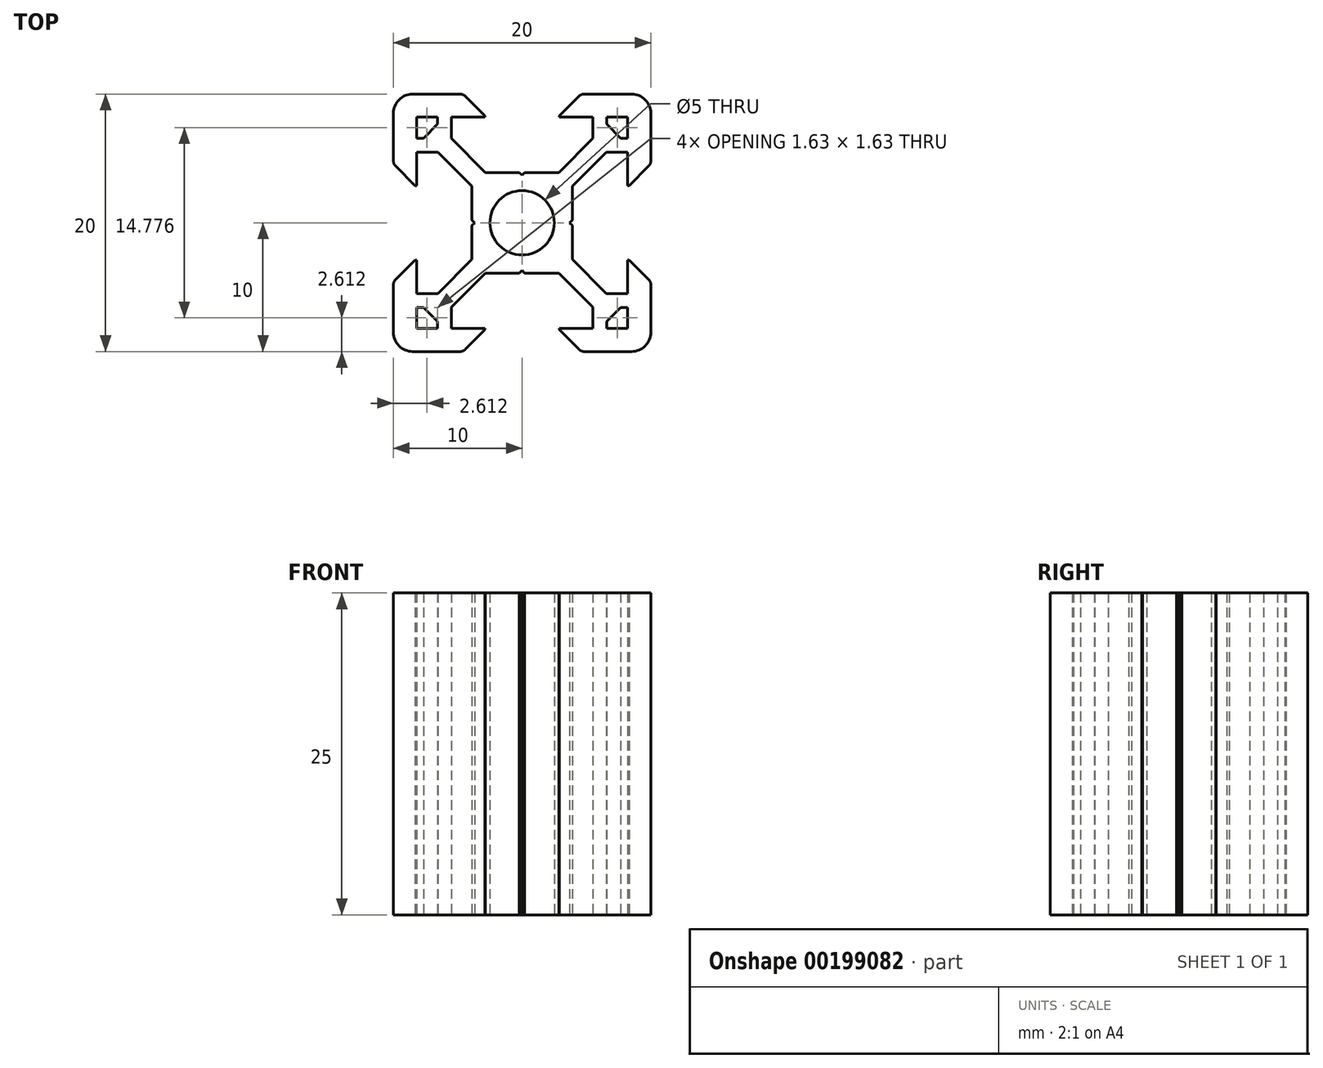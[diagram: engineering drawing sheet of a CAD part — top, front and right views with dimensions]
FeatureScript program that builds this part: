
annotation { "Feature Type Name" : "Feature", "Feature Type Description" : "" }
export const myFeature = defineFeature(function(context is Context, id is Id, definition is map)
    precondition{}
    {
        {
            var Q0;
            Q0=qCreatedBy(makeId("Top.planeOp"),FACE);
            var sketch = newSketch(context, id + "F0", { "sketchPlane" : qUnion([Q0])});
            skLineSegment(sketch, "E0.4", {"start": v(-2.85, 3.9) * mm, "end": v(-0.2, 3.9) * mm});
            skArc(sketch, "E0.48", {"start": v(-4.4, 9.82) * mm, "mid": v(-4.6, 9.95) * mm, "end": v(-4.82, 10) * mm});
            skLineSegment(sketch, "E0.49", {"start": v(-5.5, 6.55) * mm, "end": v(-2.85, 3.9) * mm});
            skLineSegment(sketch, "E0.72", {"start": v(-6.57, 7.66) * mm, "end": v(-6.57, 8.2) * mm});
            skLineSegment(sketch, "E0.103", {"start": v(-2.89, 8.2) * mm, "end": v(-5.5, 8.2) * mm});
            skArc(sketch, "E0.110", {"start": v(-8.5, 10) * mm, "mid": v(-9.07, 9.89) * mm, "end": v(-9.56, 9.56) * mm});
            skLineSegment(sketch, "E0.124", {"start": v(-5.5, 8.2) * mm, "end": v(-5.5, 6.55) * mm});
            skLineSegment(sketch, "E0.201", {"start": v(-4.4, 9.82) * mm, "end": v(-2.89, 8.3) * mm});
            skCircle(sketch, "E0.222", {"center": v(0, 0) * mm, "radius": 2.5 * mm});
            skLineSegment(sketch, "E0.289", {"start": v(-8.5, 10) * mm, "end": v(-4.82, 10) * mm});
            skLineSegment(sketch, "E0.340", {"start": v(-2.89, 8.3) * mm, "end": v(-2.89, 8.2) * mm});
            skLineSegment(sketch, "E0.361", {"start": v(-6.57, 8.2) * mm, "end": v(-8.2, 8.2) * mm});
            skLineSegment(sketch, "E0.440", {"start": v(-0.2, 3.9) * mm, "end": v(0, 3.7) * mm});
            skLineSegment(sketch, "E1", {"start": v(0, 0) * mm, "end": v(-19.3, 19.3) * mm, "construction": true});
            skLineSegment(sketch, "E2", {"start": v(-6.57, 7.66) * mm, "end": v(-7.12, 7.12) * mm});
            skLineSegment(sketch, "E3.MirrorCS", {"start": v(-8.3, 2.89) * mm, "end": v(-8.2, 2.89) * mm});
            skLineSegment(sketch, "E4.MirrorCS", {"start": v(-3.9, 0.2) * mm, "end": v(-3.7, 0) * mm});
            skLineSegment(sketch, "E5.MirrorCS", {"start": v(-10, 8.5) * mm, "end": v(-10, 4.82) * mm});
            skLineSegment(sketch, "E6.MirrorCS", {"start": v(-9.82, 4.4) * mm, "end": v(-8.3, 2.89) * mm});
            skLineSegment(sketch, "E7.MirrorCS", {"start": v(-3.9, 2.85) * mm, "end": v(-3.9, 0.2) * mm});
            skLineSegment(sketch, "E8.MirrorCS", {"start": v(-8.2, 5.5) * mm, "end": v(-6.55, 5.5) * mm});
            skLineSegment(sketch, "E9.MirrorCS", {"start": v(-8.2, 6.57) * mm, "end": v(-8.2, 8.2) * mm});
            skLineSegment(sketch, "E10.MirrorCS", {"start": v(-7.66, 6.57) * mm, "end": v(-8.2, 6.57) * mm});
            skArc(sketch, "E11.MirrorCS", {"start": v(-9.82, 4.4) * mm, "mid": v(-9.95, 4.6) * mm, "end": v(-10, 4.82) * mm});
            skArc(sketch, "E12.MirrorCS", {"start": v(-10, 8.5) * mm, "mid": v(-9.89, 9.07) * mm, "end": v(-9.56, 9.56) * mm});
            skLineSegment(sketch, "E13.MirrorCS", {"start": v(-7.66, 6.57) * mm, "end": v(-7.12, 7.12) * mm});
            skLineSegment(sketch, "E14.MirrorCS", {"start": v(-8.2, 2.89) * mm, "end": v(-8.2, 5.5) * mm});
            skLineSegment(sketch, "E15.MirrorCS", {"start": v(-6.55, 5.5) * mm, "end": v(-3.9, 2.85) * mm});
            skLineSegment(sketch, "E16", {"start": v(0, 0) * mm, "end": v(0, 23.95) * mm, "construction": true});
            skLineSegment(sketch, "E17.MirrorCS", {"start": v(6.57, 7.66) * mm, "end": v(6.57, 8.2) * mm});
            skLineSegment(sketch, "E18.MirrorCS", {"start": v(2.89, 8.3) * mm, "end": v(2.89, 8.2) * mm});
            skLineSegment(sketch, "E19.MirrorCS", {"start": v(7.66, 6.57) * mm, "end": v(7.12, 7.12) * mm});
            skArc(sketch, "E20.MirrorCS", {"start": v(9.82, 4.4) * mm, "mid": v(9.95, 4.6) * mm, "end": v(10, 4.82) * mm});
            skLineSegment(sketch, "E21.MirrorCS", {"start": v(0.2, 3.9) * mm, "end": v(0, 3.7) * mm});
            skLineSegment(sketch, "E22.MirrorCS", {"start": v(7.66, 6.57) * mm, "end": v(8.2, 6.57) * mm});
            skLineSegment(sketch, "E23.MirrorCS", {"start": v(6.57, 7.66) * mm, "end": v(7.12, 7.12) * mm});
            skArc(sketch, "E24.MirrorCS", {"start": v(4.4, 9.82) * mm, "mid": v(4.6, 9.95) * mm, "end": v(4.82, 10) * mm});
            skLineSegment(sketch, "E25.MirrorCS", {"start": v(3.9, 0.2) * mm, "end": v(3.7, 0) * mm});
            skLineSegment(sketch, "E26.MirrorCS", {"start": v(8.3, 2.89) * mm, "end": v(8.2, 2.89) * mm});
            skLineSegment(sketch, "E27.MirrorCS", {"start": v(5.5, 8.2) * mm, "end": v(5.5, 6.55) * mm});
            skLineSegment(sketch, "E28.MirrorCS", {"start": v(9.82, 4.4) * mm, "end": v(8.3, 2.89) * mm});
            skLineSegment(sketch, "E29.MirrorCS", {"start": v(8.2, 6.57) * mm, "end": v(8.2, 8.2) * mm});
            skLineSegment(sketch, "E30.MirrorCS", {"start": v(5.5, 6.55) * mm, "end": v(2.85, 3.9) * mm});
            skLineSegment(sketch, "E31.MirrorCS", {"start": v(2.89, 8.2) * mm, "end": v(5.5, 8.2) * mm});
            skLineSegment(sketch, "E32.MirrorCS", {"start": v(4.4, 9.82) * mm, "end": v(2.89, 8.3) * mm});
            skLineSegment(sketch, "E33.MirrorCS", {"start": v(3.9, 2.85) * mm, "end": v(3.9, 0.2) * mm});
            skLineSegment(sketch, "E34.MirrorCS", {"start": v(8.2, 2.89) * mm, "end": v(8.2, 5.5) * mm});
            skLineSegment(sketch, "E35.MirrorCS", {"start": v(2.85, 3.9) * mm, "end": v(0.2, 3.9) * mm});
            skLineSegment(sketch, "E36.MirrorCS", {"start": v(8.5, 10) * mm, "end": v(4.82, 10) * mm});
            skLineSegment(sketch, "E37.MirrorCS", {"start": v(10, 8.5) * mm, "end": v(10, 4.82) * mm});
            skLineSegment(sketch, "E38.MirrorCS", {"start": v(6.57, 8.2) * mm, "end": v(8.2, 8.2) * mm});
            skArc(sketch, "E39.MirrorCS", {"start": v(10, 8.5) * mm, "mid": v(9.89, 9.07) * mm, "end": v(9.56, 9.56) * mm});
            skLineSegment(sketch, "E40.MirrorCS", {"start": v(6.55, 5.5) * mm, "end": v(3.9, 2.85) * mm});
            skArc(sketch, "E41.MirrorCS", {"start": v(8.5, 10) * mm, "mid": v(9.07, 9.89) * mm, "end": v(9.56, 9.56) * mm});
            skLineSegment(sketch, "E42.MirrorCS", {"start": v(8.2, 5.5) * mm, "end": v(6.55, 5.5) * mm});
            skLineSegment(sketch, "E43", {"start": v(0, 0) * mm, "end": v(-19.98, 0) * mm, "construction": true});
            skLineSegment(sketch, "E44.MirrorCS", {"start": v(-8.3, -2.89) * mm, "end": v(-8.2, -2.89) * mm});
            skLineSegment(sketch, "E45.MirrorCS", {"start": v(0.2, -3.9) * mm, "end": v(0, -3.7) * mm});
            skLineSegment(sketch, "E46.MirrorCS", {"start": v(-0.2, -3.9) * mm, "end": v(0, -3.7) * mm});
            skLineSegment(sketch, "E47.MirrorCS", {"start": v(-2.89, -8.3) * mm, "end": v(-2.89, -8.2) * mm});
            skLineSegment(sketch, "E48.MirrorCS", {"start": v(-6.57, -7.66) * mm, "end": v(-6.57, -8.2) * mm});
            skLineSegment(sketch, "E49.MirrorCS", {"start": v(7.66, -6.57) * mm, "end": v(7.12, -7.12) * mm});
            skLineSegment(sketch, "E50.MirrorCS", {"start": v(7.66, -6.57) * mm, "end": v(8.2, -6.57) * mm});
            skArc(sketch, "E51.MirrorCS", {"start": v(9.82, -4.4) * mm, "mid": v(9.95, -4.6) * mm, "end": v(10, -4.82) * mm});
            skArc(sketch, "E52.MirrorCS", {"start": v(4.4, -9.82) * mm, "mid": v(4.6, -9.95) * mm, "end": v(4.82, -10) * mm});
            skArc(sketch, "E53.MirrorCS", {"start": v(-9.82, -4.4) * mm, "mid": v(-9.95, -4.6) * mm, "end": v(-10, -4.82) * mm});
            skArc(sketch, "E54.MirrorCS", {"start": v(-4.4, -9.82) * mm, "mid": v(-4.6, -9.95) * mm, "end": v(-4.82, -10) * mm});
            skLineSegment(sketch, "E55.MirrorCS", {"start": v(8.3, -2.89) * mm, "end": v(8.2, -2.89) * mm});
            skLineSegment(sketch, "E56.MirrorCS", {"start": v(-7.66, -6.57) * mm, "end": v(-8.2, -6.57) * mm});
            skLineSegment(sketch, "E57.MirrorCS", {"start": v(-7.66, -6.57) * mm, "end": v(-7.12, -7.12) * mm});
            skLineSegment(sketch, "E58.MirrorCS", {"start": v(2.89, -8.3) * mm, "end": v(2.89, -8.2) * mm});
            skLineSegment(sketch, "E59.MirrorCS", {"start": v(-3.9, -0.2) * mm, "end": v(-3.7, 0) * mm});
            skLineSegment(sketch, "E60.MirrorCS", {"start": v(6.57, -7.66) * mm, "end": v(6.57, -8.2) * mm});
            skLineSegment(sketch, "E61.MirrorCS", {"start": v(-6.57, -7.66) * mm, "end": v(-7.12, -7.12) * mm});
            skLineSegment(sketch, "E62.MirrorCS", {"start": v(3.9, -0.2) * mm, "end": v(3.7, 0) * mm});
            skLineSegment(sketch, "E63.MirrorCS", {"start": v(6.57, -7.66) * mm, "end": v(7.12, -7.12) * mm});
            skLineSegment(sketch, "E64.MirrorCS", {"start": v(-5.5, -8.2) * mm, "end": v(-5.5, -6.55) * mm});
            skArc(sketch, "E65.MirrorCS", {"start": v(-10, -8.5) * mm, "mid": v(-9.89, -9.07) * mm, "end": v(-9.56, -9.56) * mm});
            skLineSegment(sketch, "E66.MirrorCS", {"start": v(-9.82, -4.4) * mm, "end": v(-8.3, -2.89) * mm});
            skLineSegment(sketch, "E67.MirrorCS", {"start": v(8.2, -6.57) * mm, "end": v(8.2, -8.2) * mm});
            skLineSegment(sketch, "E68.MirrorCS", {"start": v(-10, -8.5) * mm, "end": v(-10, -4.82) * mm});
            skLineSegment(sketch, "E69.MirrorCS", {"start": v(5.5, -8.2) * mm, "end": v(5.5, -6.55) * mm});
            skLineSegment(sketch, "E70.MirrorCS", {"start": v(-6.57, -8.2) * mm, "end": v(-8.2, -8.2) * mm});
            skLineSegment(sketch, "E71.MirrorCS", {"start": v(-2.89, -8.2) * mm, "end": v(-5.5, -8.2) * mm});
            skLineSegment(sketch, "E72.MirrorCS", {"start": v(5.5, -6.55) * mm, "end": v(2.85, -3.9) * mm});
            skLineSegment(sketch, "E73.MirrorCS", {"start": v(3.9, -2.85) * mm, "end": v(3.9, -0.2) * mm});
            skLineSegment(sketch, "E74.MirrorCS", {"start": v(-3.9, -2.85) * mm, "end": v(-3.9, -0.2) * mm});
            skLineSegment(sketch, "E75.MirrorCS", {"start": v(8.2, -5.5) * mm, "end": v(6.55, -5.5) * mm});
            skLineSegment(sketch, "E76.MirrorCS", {"start": v(2.85, -3.9) * mm, "end": v(0.2, -3.9) * mm});
            skLineSegment(sketch, "E77.MirrorCS", {"start": v(10, -8.5) * mm, "end": v(10, -4.82) * mm});
            skLineSegment(sketch, "E78.MirrorCS", {"start": v(8.5, -10) * mm, "end": v(4.82, -10) * mm});
            skLineSegment(sketch, "E79.MirrorCS", {"start": v(-6.55, -5.5) * mm, "end": v(-3.9, -2.85) * mm});
            skLineSegment(sketch, "E80.MirrorCS", {"start": v(2.89, -8.2) * mm, "end": v(5.5, -8.2) * mm});
            skLineSegment(sketch, "E81.MirrorCS", {"start": v(-4.4, -9.82) * mm, "end": v(-2.89, -8.3) * mm});
            skArc(sketch, "E82.MirrorCS", {"start": v(-8.5, -10) * mm, "mid": v(-9.07, -9.89) * mm, "end": v(-9.56, -9.56) * mm});
            skLineSegment(sketch, "E83.MirrorCS", {"start": v(-2.85, -3.9) * mm, "end": v(-0.2, -3.9) * mm});
            skLineSegment(sketch, "E84.MirrorCS", {"start": v(-8.2, -2.89) * mm, "end": v(-8.2, -5.5) * mm});
            skArc(sketch, "E85.MirrorCS", {"start": v(8.5, -10) * mm, "mid": v(9.07, -9.89) * mm, "end": v(9.56, -9.56) * mm});
            skLineSegment(sketch, "E86.MirrorCS", {"start": v(8.2, -2.89) * mm, "end": v(8.2, -5.5) * mm});
            skLineSegment(sketch, "E87.MirrorCS", {"start": v(-8.2, -6.57) * mm, "end": v(-8.2, -8.2) * mm});
            skLineSegment(sketch, "E88.MirrorCS", {"start": v(9.82, -4.4) * mm, "end": v(8.3, -2.89) * mm});
            skLineSegment(sketch, "E89.MirrorCS", {"start": v(4.4, -9.82) * mm, "end": v(2.89, -8.3) * mm});
            skLineSegment(sketch, "E90.MirrorCS", {"start": v(6.55, -5.5) * mm, "end": v(3.9, -2.85) * mm});
            skLineSegment(sketch, "E91.MirrorCS", {"start": v(-8.2, -5.5) * mm, "end": v(-6.55, -5.5) * mm});
            skLineSegment(sketch, "E92.MirrorCS", {"start": v(6.57, -8.2) * mm, "end": v(8.2, -8.2) * mm});
            skLineSegment(sketch, "E93.MirrorCS", {"start": v(-8.5, -10) * mm, "end": v(-4.82, -10) * mm});
            skLineSegment(sketch, "E94.MirrorCS", {"start": v(-5.5, -6.55) * mm, "end": v(-2.85, -3.9) * mm});
            skArc(sketch, "E95.MirrorCS", {"start": v(10, -8.5) * mm, "mid": v(9.89, -9.07) * mm, "end": v(9.56, -9.56) * mm});
            skSolve(sketch);
        }
        {
            var Q0;
            Q0=qSketchRegion(id+"F0",true);
            extrude(context, id + "F1", {"entities" : qUnion([Q0]), "depth" : 25 * mm});
        }
    });
